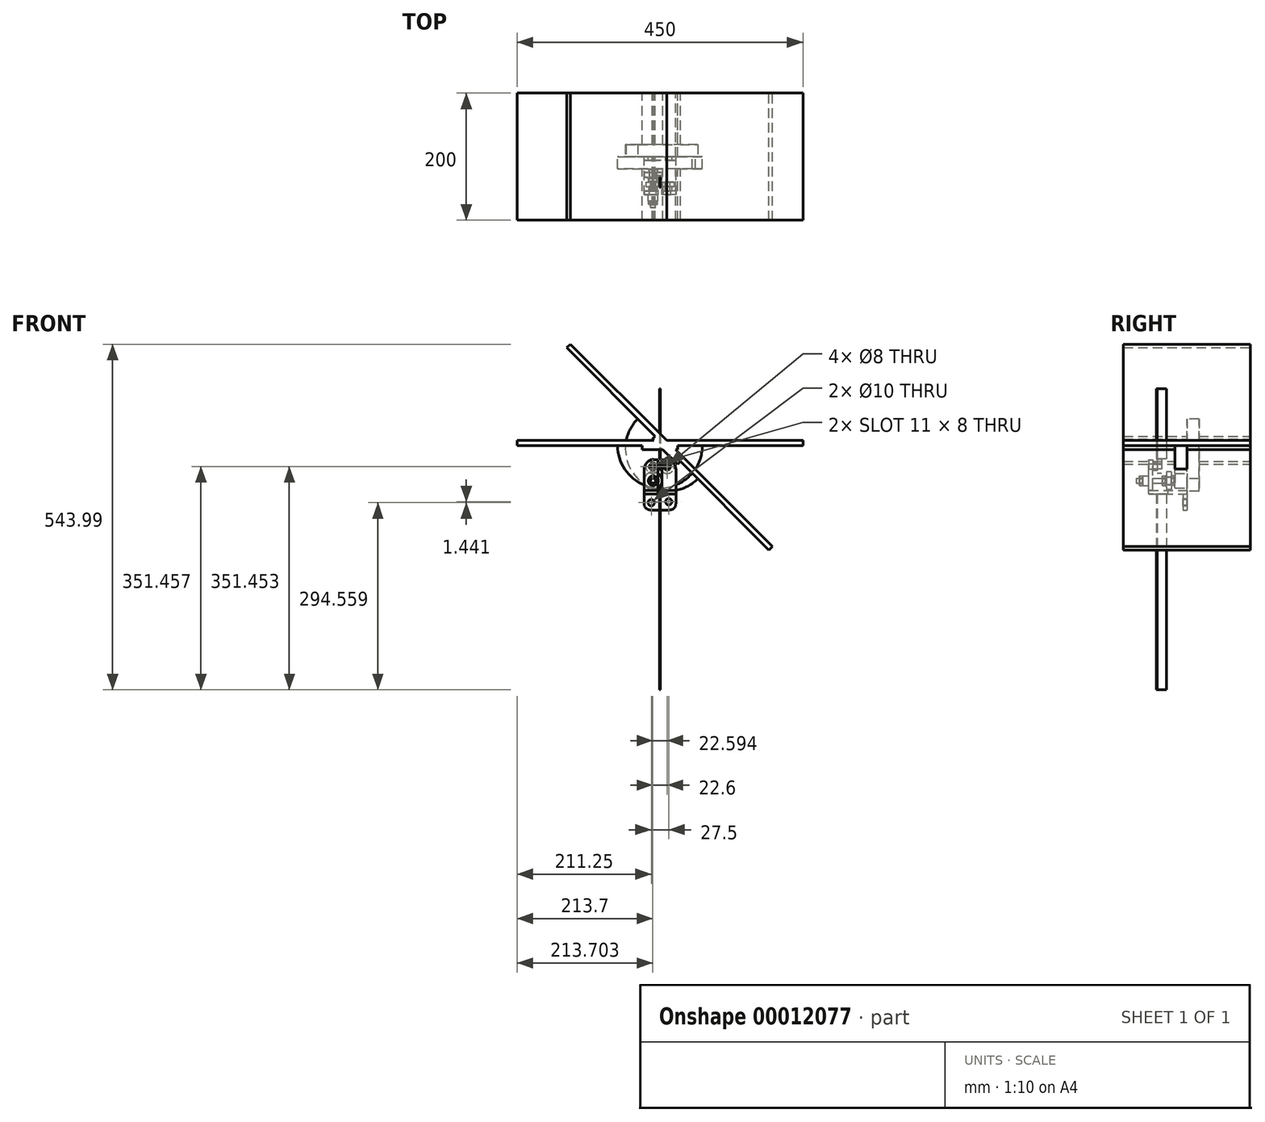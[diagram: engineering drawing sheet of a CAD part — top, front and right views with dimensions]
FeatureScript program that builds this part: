
annotation { "Feature Type Name" : "Feature", "Feature Type Description" : "" }
export const myFeature = defineFeature(function(context is Context, id is Id, definition is map)
    precondition{}
    {
        {
            var Q0;
            Q0=qCreatedBy(makeId("Front.planeOp"),FACE);
            var sketch = newSketch(context, id + "F0", { "sketchPlane" : qUnion([Q0])});
            skLineSegment(sketch, "E0", {"start": v(0, 0) * mm, "end": v(-160.58, 0) * mm, "construction": true});
            skLineSegment(sketch, "E1", {"start": v(-147.95, 0) * mm, "end": v(-147.95, 211) * mm, "construction": true});
            skLineSegment(sketch, "E2", {"start": v(-147.95, 211) * mm, "end": v(0, 367) * mm, "construction": true});
            skLineSegment(sketch, "E3", {"start": v(0, 367) * mm, "end": v(0, 0) * mm, "construction": true});
            skLineSegment(sketch, "E4", {"start": v(-28, 378) * mm, "end": v(28, 378) * mm, "construction": true});
            skLineSegment(sketch, "E5", {"start": v(-225, 384.3) * mm, "end": v(-28, 384.3) * mm, "construction": true});
            skLineSegment(sketch, "E6", {"start": v(28, 384.3) * mm, "end": v(28, 378) * mm, "construction": true});
            skLineSegment(sketch, "E7", {"start": v(-28, 384.3) * mm, "end": v(-28, 378) * mm, "construction": true});
            skLineSegment(sketch, "E8", {"start": v(-225, 392.3) * mm, "end": v(225, 392.3) * mm, "construction": true});
            skLineSegment(sketch, "E9", {"start": v(225, 392.3) * mm, "end": v(225, 384.3) * mm, "construction": true});
            skLineSegment(sketch, "E10", {"start": v(-225, 392.3) * mm, "end": v(-225, 384.3) * mm, "construction": true});
            skLineSegment(sketch, "E11.trimOffspring", {"start": v(28, 384.3) * mm, "end": v(225, 384.3) * mm, "construction": true});
            skCircle(sketch, "E12", {"center": v(0, 367) * mm, "radius": 4 * mm});
            skCircle(sketch, "E13", {"center": v(-147.95, 211) * mm, "radius": 155 * mm});
            skSolve(sketch);
        }
        {
            var Q0;
            Q0=qCreatedBy(makeId("Front.planeOp"),FACE);
            var sketch = newSketch(context, id + "F1", { "sketchPlane" : qUnion([Q0])});
            skLineSegment(sketch, "E14.0", {"start": v(-225, 392.3) * mm, "end": v(225, 392.3) * mm});
            skLineSegment(sketch, "E14.1", {"start": v(-225, 384.3) * mm, "end": v(-28, 384.3) * mm});
            skLineSegment(sketch, "E14.2", {"start": v(-28, 378) * mm, "end": v(28, 378) * mm});
            skLineSegment(sketch, "E14.3", {"start": v(28, 384.3) * mm, "end": v(225, 384.3) * mm});
            skLineSegment(sketch, "E14.4", {"start": v(-225, 392.3) * mm, "end": v(-225, 384.3) * mm});
            skLineSegment(sketch, "E14.5", {"start": v(-28, 384.3) * mm, "end": v(-28, 378) * mm});
            skLineSegment(sketch, "E14.6", {"start": v(28, 384.3) * mm, "end": v(28, 378) * mm});
            skLineSegment(sketch, "E14.7", {"start": v(225, 392.3) * mm, "end": v(225, 384.3) * mm});
            skSolve(sketch);
        }
        {
            var Q0;
            Q0 = qSketchRegion(id + "F1", true);
            var Q1;
            Q1 = qConstructionFilter(qBodyType(qCreatedBy(id + "F1" ,EDGE), BodyType.WIRE), ConstructionObject.NO);
            extrude(context, id + "F2", {"entities" : qUnion([Q0]), "surfaceEntities" : qUnion([Q1]), "depth" : 100 * mm, "hasSecondDirection" : true, "secondDirectionOppositeDirection" : true, "secondDirectionDepth" : 100 * mm});
        }
        {
            var Q0;
            Q0=qCreatedBy(makeId("Front.planeOp"),FACE);
            var sketch = newSketch(context, id + "F3", { "sketchPlane" : qUnion([Q0])});
            skLineSegment(sketch, "E15.1", {"start": v(-225, 392.3) * mm, "end": v(-225, 384.3) * mm});
            skLineSegment(sketch, "E16.7.0", {"start": v(32.03, 359.43) * mm, "end": v(171.33, 220.13) * mm});
            skLineSegment(sketch, "E16.7.1", {"start": v(-12.02, 394.58) * mm, "end": v(27.58, 354.98) * mm});
            skLineSegment(sketch, "E16.7.2", {"start": v(-141.2, 543.99) * mm, "end": v(176.99, 225.8) * mm});
            skLineSegment(sketch, "E16.7.3", {"start": v(-146.87, 538.33) * mm, "end": v(-7.57, 399.03) * mm});
            skLineSegment(sketch, "E16.7.5", {"start": v(32.03, 359.43) * mm, "end": v(27.58, 354.98) * mm});
            skLineSegment(sketch, "E16.7.6", {"start": v(-141.2, 543.99) * mm, "end": v(-146.87, 538.33) * mm});
            skLineSegment(sketch, "E16.7.7", {"start": v(176.99, 225.8) * mm, "end": v(171.33, 220.13) * mm});
            skLineSegment(sketch, "E16.7.8", {"start": v(-7.57, 399.03) * mm, "end": v(-12.02, 394.58) * mm});
            skPoint(sketch, "E16.center", {"position": v(0, 367) * mm});
            skSolve(sketch);
        }
        {
            var Q0;
            Q0 = qSketchRegion(id + "F3", true);
            extrude(context, id + "F4", {"entities" : qUnion([Q0]), "depth" : 100 * mm, "hasSecondDirection" : true, "secondDirectionOppositeDirection" : true, "secondDirectionDepth" : 100 * mm});
        }
        {
            var Q0;
            Q0=qCreatedBy(makeId("Top.planeOp"),FACE);
            var sketch = newSketch(context, id + "F5", { "sketchPlane" : qUnion([Q0])});
            skLineSegment(sketch, "E17.0", {"start": v(0.3, -47.03) * mm, "end": v(0.3, -32.5) * mm});
            skLineSegment(sketch, "E18.0", {"start": v(-0.3, -47.03) * mm, "end": v(-0.3, -32.5) * mm});
            skLineSegment(sketch, "E19", {"start": v(-0.3, -32.5) * mm, "end": v(0.3, -32.5) * mm});
            skLineSegment(sketch, "E20", {"start": v(0.3, -47.03) * mm, "end": v(0.54, -48.4) * mm});
            skLineSegment(sketch, "E21.MirrorCS", {"start": v(-0.3, -47.03) * mm, "end": v(-0.54, -48.4) * mm});
            skLineSegment(sketch, "E22", {"start": v(0, -48.5) * mm, "end": v(0.54, -48.4) * mm});
            skLineSegment(sketch, "E23", {"start": v(0, -48.5) * mm, "end": v(-0.54, -48.4) * mm});
            skSolve(sketch);
        }
        {
            var Q0;
            Q0 = qSketchRegion(id + "F5", true);
            extrude(context, id + "F6", {"entities" : qUnion([Q0]), "depth" : 474 * mm});
        }
        {
            var Q0;
            Q0=qCreatedBy(makeId("Front.planeOp"),FACE);
            var sketch = newSketch(context, id + "F7", { "sketchPlane" : qUnion([Q0])});
            skLineSegment(sketch, "E24.0", {"start": v(-15, 282.96) * mm, "end": v(15, 282.96) * mm});
            skLineSegment(sketch, "E24.1", {"start": v(-25, 308) * mm, "end": v(-25, 292.96) * mm});
            skLineSegment(sketch, "E24.2", {"start": v(25, 308) * mm, "end": v(25, 292.96) * mm});
            skLineSegment(sketch, "E24.3", {"start": v(25, 308) * mm, "end": v(-25, 308) * mm});
            skCircle(sketch, "E24.4", {"center": v(13.75, 296) * mm, "radius": 5 * mm});
            skCircle(sketch, "E24.5", {"center": v(-13.75, 294.56) * mm, "radius": 5 * mm});
            skArc(sketch, "E25.filletArc", {"start": v(-25, 292.96) * mm, "mid": v(-22.07, 285.9) * mm, "end": v(-15, 282.96) * mm});
            skArc(sketch, "E26.filletArc", {"start": v(15, 282.96) * mm, "mid": v(22.07, 285.9) * mm, "end": v(25, 292.96) * mm});
            skSolve(sketch);
        }
        {
            var Q0;
            Q0 = qSketchRegion(id + "F7", true);
            extrude(context, id + "F8", {"entities" : qUnion([Q0]), "depth" : 6 * mm});
        }
        {
            var Q0;
            Q0=qCreatedBy(makeId("Front.planeOp"),FACE);
            var sketch = newSketch(context, id + "F9", { "sketchPlane" : qUnion([Q0])});
            skLineSegment(sketch, "E27.0", {"start": v(25, 308) * mm, "end": v(-25, 308) * mm});
            skLineSegment(sketch, "E28", {"start": v(-25, 308) * mm, "end": v(-25, 314) * mm});
            skLineSegment(sketch, "E29", {"start": v(-25, 314) * mm, "end": v(25, 314) * mm});
            skLineSegment(sketch, "E30", {"start": v(25, 314) * mm, "end": v(25, 308) * mm});
            skPoint(sketch, "E31.orphan", {"position": v(25, 315.71) * mm});
            skSolve(sketch);
        }
        {
            var Q0;
            Q0 = qSketchRegion(id + "F9", true);
            extrude(context, id + "F10", {"entities" : qUnion([Q0]), "depth" : 60 * mm});
        }
        {
            var Q0;
            Q0=makeQuery(id+"F10.opExtrude","CAP_FACE",FACE,{"disambiguationData":[OSD([sQuery(id+"F9.wireOp",EDGE,"E27.0"),sQuery(id+"F9.wireOp",EDGE,"E28"),sQuery(id+"F9.wireOp",EDGE,"E29"),sQuery(id+"F9.wireOp",EDGE,"E30")])],"isStart":false});
            var sketch = newSketch(context, id + "F11", { "sketchPlane" : qUnion([Q0])});
            skLineSegment(sketch, "E32.0", {"start": v(-25, 314) * mm, "end": v(25, 314) * mm});
            skLineSegment(sketch, "E33", {"start": v(-25, 314) * mm, "end": v(-25, 347) * mm});
            skLineSegment(sketch, "E34", {"start": v(25, 314) * mm, "end": v(25, 347) * mm});
            skLineSegment(sketch, "E35", {"start": v(10, 362) * mm, "end": v(-10, 362) * mm});
            skPoint(sketch, "E36.visualSharp", {"position": v(-25, 362) * mm});
            skArc(sketch, "E36.filletArc", {"start": v(-10, 362) * mm, "mid": v(-20.6, 357.6) * mm, "end": v(-25, 347) * mm});
            skPoint(sketch, "E37.visualSharp", {"position": v(25, 362) * mm});
            skArc(sketch, "E37.filletArc", {"start": v(25, 347) * mm, "mid": v(20.6, 357.6) * mm, "end": v(10, 362) * mm});
            skSolve(sketch);
        }
        {
            var Q0;
            Q0 = qSketchRegion(id + "F11", true);
            extrude(context, id + "F12", {"entities" : qUnion([Q0]), "oppositeDirection" : true, "depth" : 6 * mm});
        }
        {
            var Q0;
            Q0=makeQuery(id+"F10.opExtrude","CAP_FACE",FACE,{"disambiguationData":[OSD([sQuery(id+"F9.wireOp",EDGE,"E27.0"),sQuery(id+"F9.wireOp",EDGE,"E28"),sQuery(id+"F9.wireOp",EDGE,"E29"),sQuery(id+"F9.wireOp",EDGE,"E30")])],"isStart":false});
            var sketch = newSketch(context, id + "F13", { "sketchPlane" : qUnion([Q0])});
            skLineSegment(sketch, "E38.0", {"start": v(3, 308) * mm, "end": v(-3, 308) * mm});
            skLineSegment(sketch, "E39.0", {"start": v(3, 308) * mm, "end": v(3, 363.2) * mm});
            skLineSegment(sketch, "E40.0", {"start": v(-3, 308) * mm, "end": v(-3, 363.2) * mm});
            skLineSegment(sketch, "E41", {"start": v(-3, 363.2) * mm, "end": v(3, 363.2) * mm});
            skPoint(sketch, "E42.start.orphan", {"position": v(0, 308) * mm});
            skPoint(sketch, "E43.orphan", {"position": v(25, 308) * mm});
            skPoint(sketch, "E44.orphan", {"position": v(-25, 308) * mm});
            skSolve(sketch);
        }
        {
            var Q0;
            Q0 = qSketchRegion(id + "F13", true);
            extrude(context, id + "F14", {"entities" : qUnion([Q0]), "operationType" : NewBodyOperationType.REMOVE, "oppositeDirection" : true, "depth" : 30 * mm});
        }
        {
            var Q0;
            {var subQ0=sQuery(id+"F11.wireOp",EDGE,"E32.0");var subQ1=sQuery(id+"F11.wireOp",EDGE,"E35");var subQ2=sQuery(id+"F11.wireOp",EDGE,"E33");Q0=makeQuery(id+"F14.boolean.opBoolean","SPLIT",FACE,{"disambiguationData":[TD([makeQuery(id+"F12.opExtrude","SWEPT_FACE",FACE,{"disambiguationData":[OSD([subQ2])]})])],"derivedFrom":makeQuery(id+"F12.opExtrude","CAP_FACE",FACE,{"disambiguationData":[OSD([subQ0,subQ2,sQuery(id+"F11.wireOp",EDGE,"E34"),subQ1])],"isStart":false})});}
            var sketch = newSketch(context, id + "F15", { "sketchPlane" : qUnion([Q0])});
            skCircle(sketch, "E45", {"center": v(10.92, 329) * mm, "radius": 3.4 * mm});
            skCircle(sketch, "E46", {"center": v(10.92, 329) * mm, "radius": 7.5 * mm});
            skSolve(sketch);
        }
        {
            var Q0;
            Q0 = qSketchRegion(id + "F15", true);
            extrude(context, id + "F16", {"entities" : qUnion([Q0]), "oppositeDirection" : true, "depth" : 16 * mm, "hasSecondDirection" : true, "secondDirectionOppositeDirection" : true, "secondDirectionDepth" : 6 * mm});
        }
        {
            var Q0;
            {var subQ0=sQuery(id+"F11.wireOp",EDGE,"E32.0");var subQ1=sQuery(id+"F11.wireOp",EDGE,"E33");var subQ2=sQuery(id+"F11.wireOp",EDGE,"E35");Q0=makeQuery(id+"F14.boolean.opBoolean","SPLIT",FACE,{"disambiguationData":[TD([makeQuery(id+"F12.opExtrude","SWEPT_FACE",FACE,{"disambiguationData":[OSD([subQ1])]})])],"derivedFrom":makeQuery(id+"F12.opExtrude","CAP_FACE",FACE,{"disambiguationData":[OSD([subQ0,subQ1,sQuery(id+"F11.wireOp",EDGE,"E34"),subQ2])],"isStart":false})});}
            var sketch = newSketch(context, id + "F17", { "sketchPlane" : qUnion([Q0])});
            skLineSegment(sketch, "E47.0", {"start": v(46.96, 425.27) * mm, "end": v(-19.08, 359.24) * mm});
            skPoint(sketch, "E48.endSnap0", {"position": v(0, 362) * mm});
            skCircle(sketch, "E49", {"center": v(11.3, 351.46) * mm, "radius": 11 * mm});
            skLineSegment(sketch, "E50.0", {"start": v(0.3, 308) * mm, "end": v(0.3, 373.94) * mm});
            skLineSegment(sketch, "E51.0", {"start": v(-0.3, 308) * mm, "end": v(-0.3, 373.94) * mm});
            skLineSegment(sketch, "E52.0", {"start": v(0, 308) * mm, "end": v(0, 373.94) * mm});
            skCircle(sketch, "E53.MirrorC", {"center": v(-11.3, 351.46) * mm, "radius": 11 * mm});
            skCircle(sketch, "E54", {"center": v(-11.3, 351.46) * mm, "radius": 4 * mm});
            skCircle(sketch, "E55", {"center": v(11.3, 351.46) * mm, "radius": 4 * mm});
            skSolve(sketch);
        }
        {
            var Q0;
            Q0 = qSketchRegion(id + "F17", true);
            extrude(context, id + "F18", {"entities" : qUnion([Q0]), "depth" : 14 * mm, "hasSecondDirection" : true, "secondDirectionOppositeDirection" : false, "secondDirectionDepth" : 7 * mm});
        }
        {
            var Q0;
            Q0=makeQuery(id+"F6.opExtrude","SWEPT_FACE",FACE,{"disambiguationData":[OSD([sQuery(id+"F5.wireOp",EDGE,"E19")])]});
            var sketch = newSketch(context, id + "F19", { "sketchPlane" : qUnion([Q0])});
            skCircle(sketch, "E56", {"center": v(10.92, 329) * mm, "radius": 6 * mm});
            skCircle(sketch, "E57", {"center": v(10.92, 329) * mm, "radius": 14 * mm});
            skSolve(sketch);
        }
        {
            var Q0;
            Q0 = qSketchRegion(id + "F19", true);
            extrude(context, id + "F20", {"entities" : qUnion([Q0]), "depth" : 8 * mm});
        }
        {
            var Q0;
            {var subQ0=sQuery(id+"F11.wireOp",EDGE,"E36.filletArc");var subQ1=sQuery(id+"F11.wireOp",EDGE,"E33");var subQ2=sQuery(id+"F11.wireOp",EDGE,"E35");var subQ3=sQuery(id+"F11.wireOp",EDGE,"E32.0");Q0=makeQuery(id+"F14.boolean.opBoolean","SPLIT",FACE,{"disambiguationData":[TD([makeQuery(id+"F12.opExtrude","SWEPT_FACE",FACE,{"disambiguationData":[OSD([subQ1])]})])],"derivedFrom":makeQuery(id+"F12.opExtrude","CAP_FACE",FACE,{"disambiguationData":[OSD([subQ3,subQ1,sQuery(id+"F11.wireOp",EDGE,"E34"),subQ2,subQ0,sQuery(id+"F11.wireOp",EDGE,"E37.filletArc")])],"isStart":false})});}
            var sketch = newSketch(context, id + "F21", { "sketchPlane" : qUnion([Q0])});
            skCircle(sketch, "E58.1", {"center": v(10.92, 329) * mm, "radius": 3.4 * mm});
            skLineSegment(sketch, "E59", {"start": v(11.3, 347.74) * mm, "end": v(11.3, 347.74) * mm});
            skLineSegment(sketch, "E60", {"start": v(11.3, 355.16) * mm, "end": v(11.3, 355.16) * mm});
            skLineSegment(sketch, "E61", {"start": v(12.8, 355.45) * mm, "end": v(9.8, 355.45) * mm});
            skLineSegment(sketch, "E62", {"start": v(9.8, 347.45) * mm, "end": v(12.8, 347.45) * mm});
            skArc(sketch, "E63.trimOffspring", {"start": v(9.8, 355.45) * mm, "mid": v(5.8, 351.45) * mm, "end": v(9.8, 347.45) * mm});
            skArc(sketch, "E64.trimOffspring", {"start": v(12.8, 347.45) * mm, "mid": v(16.8, 351.45) * mm, "end": v(12.8, 355.45) * mm});
            skArc(sketch, "E65.MirrorCS", {"start": v(-9.8, 355.45) * mm, "mid": v(-5.8, 351.45) * mm, "end": v(-9.8, 347.45) * mm});
            skLineSegment(sketch, "E66.MirrorCS", {"start": v(-12.8, 355.45) * mm, "end": v(-9.8, 355.45) * mm});
            skArc(sketch, "E67.MirrorCS", {"start": v(-12.8, 347.45) * mm, "mid": v(-16.8, 351.45) * mm, "end": v(-12.8, 355.45) * mm});
            skLineSegment(sketch, "E68.MirrorCS", {"start": v(-9.8, 347.45) * mm, "end": v(-12.8, 347.45) * mm});
            skSolve(sketch);
        }
        {
            var Q0;
            Q0 = qSketchRegion(id + "F21", true);
            extrude(context, id + "F22", {"entities" : qUnion([Q0]), "operationType" : NewBodyOperationType.REMOVE, "oppositeDirection" : true, "depth" : 25 * mm});
        }
        {
            var Q0;
            {var subQ0=sQuery(id+"F11.wireOp",EDGE,"E36.filletArc");var subQ1=sQuery(id+"F11.wireOp",EDGE,"E33");var subQ2=sQuery(id+"F11.wireOp",EDGE,"E35");var subQ3=sQuery(id+"F11.wireOp",EDGE,"E32.0");Q0=makeQuery(id+"F14.boolean.opBoolean","SPLIT",FACE,{"disambiguationData":[TD([makeQuery(id+"F12.opExtrude","SWEPT_FACE",FACE,{"disambiguationData":[OSD([subQ1])]})])],"derivedFrom":makeQuery(id+"F12.opExtrude","CAP_FACE",FACE,{"disambiguationData":[OSD([subQ3,subQ1,sQuery(id+"F11.wireOp",EDGE,"E34"),subQ2,subQ0,sQuery(id+"F11.wireOp",EDGE,"E37.filletArc")])],"isStart":false})});}
            var sketch = newSketch(context, id + "F23", { "sketchPlane" : qUnion([Q0])});
            skCircle(sketch, "E69.0", {"center": v(11.3, 351.46) * mm, "radius": 4 * mm});
            skCircle(sketch, "E69.1", {"center": v(-11.3, 351.46) * mm, "radius": 4 * mm});
            skCircle(sketch, "E70", {"center": v(11.3, 351.46) * mm, "radius": 6.75 * mm});
            skCircle(sketch, "E71", {"center": v(-11.3, 351.46) * mm, "radius": 6.75 * mm});
            skSolve(sketch);
        }
        {
            var Q0;
            Q0 = qSketchRegion(id + "F23", true);
            var Q1;
            Q1=makeQuery(id+"F18.opExtrude","CAP_FACE",FACE,{"disambiguationData":[OSD([sQuery(id+"F17.wireOp",EDGE,"E49"),sQuery(id+"F17.wireOp",EDGE,"E55")])],"isStart":true});
            extrude(context, id + "F24", {"entities" : qUnion([Q0]), "endBound" : BoundingType.UP_TO_SURFACE, "endBoundEntityFace" : qUnion([Q1]), "depth" : 25 * mm});
        }
        {
            var Q0;
            Q0=makeQuery(id+"F20.opExtrude","CAP_FACE",FACE,{"disambiguationData":[OSD([sQuery(id+"F19.wireOp",EDGE,"E56"),sQuery(id+"F19.wireOp",EDGE,"E57")])],"isStart":false});
            var sketch = newSketch(context, id + "F25", { "sketchPlane" : qUnion([Q0])});
            skCircle(sketch, "E72.cCircle", {"center": v(10.92, 329) * mm, "radius": 6.5 * mm, "construction": true});
            skLineSegment(sketch, "E72.0", {"start": v(17.73, 325.85) * mm, "end": v(11.6, 321.52) * mm});
            skLineSegment(sketch, "E72.1", {"start": v(11.6, 321.52) * mm, "end": v(4.78, 324.68) * mm});
            skLineSegment(sketch, "E72.2", {"start": v(4.78, 324.68) * mm, "end": v(4.1, 332.15) * mm});
            skLineSegment(sketch, "E72.3", {"start": v(4.1, 332.15) * mm, "end": v(10.24, 336.48) * mm});
            skLineSegment(sketch, "E72.4", {"start": v(10.24, 336.48) * mm, "end": v(17.05, 333.32) * mm});
            skLineSegment(sketch, "E72.5", {"start": v(17.05, 333.32) * mm, "end": v(17.73, 325.85) * mm});
            skPoint(sketch, "E72.0.midPoint", {"position": v(14.66, 323.69) * mm});
            skSolve(sketch);
        }
        {
            var Q0;
            Q0 = qSketchRegion(id + "F25", true);
            extrude(context, id + "F26", {"entities" : qUnion([Q0]), "depth" : 4 * mm});
        }
        {
            var Q0;
            {var subQ0=sQuery(id+"F11.wireOp",EDGE,"E32.0");Q0=makeQuery(id+"F14.boolean.opBoolean","COPY",FACE,{"disambiguationData":[TD([makeQuery(id+"F12.opExtrude","SWEPT_FACE",FACE,{"disambiguationData":[OSD([subQ0])]})])],"derivedFrom":makeQuery(id+"F14.opExtrude","SWEPT_FACE",FACE,{"disambiguationData":[OSD([sQuery(id+"F13.wireOp",EDGE,"E40.0")])]})});}
            cPlane(context, id + "F27", {"entities" : qUnion([Q0]), "cplaneType" : CPlaneType.OFFSET, "offset" : 7.92 * mm, "oppositeDirection" : true, "width" : 150 * mm, "height" : 150 * mm});
        }
        {
            var Q0;
            Q0=qCreatedBy(id+"F27.planeOp",FACE);
            var sketch = newSketch(context, id + "F28", { "sketchPlane" : qUnion([Q0])});
            skLineSegment(sketch, "E73", {"start": v(-18.7, 329) * mm, "end": v(-71.14, 329) * mm, "construction": true});
            skLineSegment(sketch, "E74", {"start": v(-24.92, 335) * mm, "end": v(-24.92, 333) * mm});
            skLineSegment(sketch, "E75", {"start": v(-24.92, 335) * mm, "end": v(-32.5, 335) * mm});
            skLineSegment(sketch, "E76.0", {"start": v(-32.5, 337.49) * mm, "end": v(-32.5, 335) * mm});
            skLineSegment(sketch, "E77", {"start": v(-32.5, 337.49) * mm, "end": v(-34.5, 337.49) * mm});
            skLineSegment(sketch, "E78", {"start": v(-34.5, 337.49) * mm, "end": v(-34.5, 333) * mm});
            skLineSegment(sketch, "E79", {"start": v(-24.92, 333) * mm, "end": v(-34.5, 333) * mm});
            skSolve(sketch);
        }
        {
            var Q0;
            Q0 = qSketchRegion(id + "F28", true);
            var Q1;
            Q1=sQuery(id+"F28.wireOp",EDGE,"E73");
            revolve(context, id + "F29", {"entities" : qUnion([Q0]), "axis" : qUnion([Q1]), "revolveType" : RevolveType.FULL});
        }
        {
            var Q0;
            Q0=makeQuery(id+"F29.opRevolve","SWEPT_FACE",FACE,{"disambiguationData":[OSD([sQuery(id+"F28.wireOp",EDGE,"E78")])]});
            var sketch = newSketch(context, id + "F30", { "sketchPlane" : qUnion([Q0])});
            skCircle(sketch, "E80.cCircle", {"center": v(-10.92, 329) * mm, "radius": 6.5 * mm, "construction": true});
            skLineSegment(sketch, "E80.0", {"start": v(-4.12, 325.82) * mm, "end": v(-10.27, 321.52) * mm});
            skLineSegment(sketch, "E80.1", {"start": v(-10.27, 321.52) * mm, "end": v(-17.07, 324.7) * mm});
            skLineSegment(sketch, "E80.2", {"start": v(-17.07, 324.7) * mm, "end": v(-17.72, 332.18) * mm});
            skLineSegment(sketch, "E80.3", {"start": v(-17.72, 332.18) * mm, "end": v(-11.57, 336.48) * mm});
            skLineSegment(sketch, "E80.4", {"start": v(-11.57, 336.48) * mm, "end": v(-4.77, 333.3) * mm});
            skLineSegment(sketch, "E80.5", {"start": v(-4.77, 333.3) * mm, "end": v(-4.12, 325.82) * mm});
            skPoint(sketch, "E80.0.midPoint", {"position": v(-7.2, 323.67) * mm});
            skCircle(sketch, "E81.0", {"center": v(-10.92, 329) * mm, "radius": 4 * mm});
            skSolve(sketch);
        }
        {
            var Q0;
            Q0 = qSketchRegion(id + "F30", true);
            extrude(context, id + "F31", {"entities" : qUnion([Q0]), "depth" : 4.5 * mm});
        }
        {
            var Q0;
            Q0=qCreatedBy(id+"F27.planeOp",FACE);
            var sketch = newSketch(context, id + "F32", { "sketchPlane" : qUnion([Q0])});
            skLineSegment(sketch, "E82", {"start": v(-24.01, 329) * mm, "end": v(-80.08, 329) * mm});
            skLineSegment(sketch, "E83", {"start": v(-24.01, 333) * mm, "end": v(-80.08, 333) * mm});
            skLineSegment(sketch, "E84", {"start": v(-24.01, 333) * mm, "end": v(-24.01, 329) * mm});
            skLineSegment(sketch, "E85", {"start": v(-80.08, 333) * mm, "end": v(-80.08, 329) * mm});
            skPoint(sketch, "E86.orphan", {"position": v(-80.08, 327.73) * mm});
            skPoint(sketch, "E87.orphan", {"position": v(-24.01, 327.73) * mm});
            skSolve(sketch);
        }
        {
            var Q0;
            Q0 = qSketchRegion(id + "F32", true);
            var Q1;
            Q1=sQuery(id+"F32.wireOp",EDGE,"E82");
            revolve(context, id + "F33", {"operationType" : NewBodyOperationType.ADD, "entities" : qUnion([Q0]), "axis" : qUnion([Q1]), "revolveType" : RevolveType.FULL});
        }
        {
            var Q0;
            Q0=makeQuery(id+"F16.opExtrude","CAP_FACE",FACE,{"disambiguationData":[OSD([sQuery(id+"F15.wireOp",EDGE,"E45"),sQuery(id+"F15.wireOp",EDGE,"E46")])],"isStart":false});
            var sketch = newSketch(context, id + "F34", { "sketchPlane" : qUnion([Q0])});
            skCircle(sketch, "E88.cCircle", {"center": v(-10.92, 329) * mm, "radius": 6.5 * mm, "construction": true});
            skLineSegment(sketch, "E88.0", {"start": v(-4.01, 326.06) * mm, "end": v(-10, 321.55) * mm});
            skLineSegment(sketch, "E88.1", {"start": v(-10, 321.55) * mm, "end": v(-16.91, 324.49) * mm});
            skLineSegment(sketch, "E88.2", {"start": v(-16.91, 324.49) * mm, "end": v(-17.82, 331.94) * mm});
            skLineSegment(sketch, "E88.3", {"start": v(-17.82, 331.94) * mm, "end": v(-11.83, 336.45) * mm});
            skLineSegment(sketch, "E88.4", {"start": v(-11.83, 336.45) * mm, "end": v(-4.92, 333.51) * mm});
            skLineSegment(sketch, "E88.5", {"start": v(-4.92, 333.51) * mm, "end": v(-4.01, 326.06) * mm});
            skPoint(sketch, "E88.0.midPoint", {"position": v(-7, 323.8) * mm});
            skSolve(sketch);
        }
        {
            var Q0;
            Q0 = qSketchRegion(id + "F34", true);
            extrude(context, id + "F35", {"entities" : qUnion([Q0]), "depth" : 5 * mm});
        }
        {
            var Q0;
            Q0=makeQuery(id+"F8.opExtrude","CAP_FACE",FACE,{"disambiguationData":[OSD([sQuery(id+"F7.wireOp",EDGE,"E24.0"),sQuery(id+"F7.wireOp",EDGE,"E24.1"),sQuery(id+"F7.wireOp",EDGE,"E24.2"),sQuery(id+"F7.wireOp",EDGE,"E24.3"),sQuery(id+"F7.wireOp",EDGE,"E24.4"),sQuery(id+"F7.wireOp",EDGE,"E24.5")])],"isStart":true});
            var sketch = newSketch(context, id + "F36", { "sketchPlane" : qUnion([Q0])});
            skLineSegment(sketch, "E89", {"start": v(27.96, 384.14) * mm, "end": v(0, 384.14) * mm, "construction": true});
            skLineSegment(sketch, "E90", {"start": v(0, 378.04) * mm, "end": v(0, 384.14) * mm, "construction": true});
            skArc(sketch, "E91", {"start": v(-66.67, 384.3) * mm, "mid": v(0, 317.47) * mm, "end": v(66.67, 384.3) * mm});
            skLineSegment(sketch, "E92.0", {"start": v(-28, 384.3) * mm, "end": v(-66.67, 384.3) * mm});
            skLineSegment(sketch, "E92.1", {"start": v(-28, 384.3) * mm, "end": v(-28, 378) * mm});
            skLineSegment(sketch, "E92.2", {"start": v(28, 378) * mm, "end": v(-28, 378) * mm});
            skLineSegment(sketch, "E92.3", {"start": v(28, 384.3) * mm, "end": v(28, 378) * mm});
            skLineSegment(sketch, "E92.4", {"start": v(66.67, 384.3) * mm, "end": v(28, 384.3) * mm});
            skPoint(sketch, "E93.orphan", {"position": v(-225, 384.3) * mm});
            skPoint(sketch, "E94.orphan", {"position": v(225, 384.3) * mm});
            skSolve(sketch);
        }
        {
            var Q0;
            Q0 = qSketchRegion(id + "F36", true);
            extrude(context, id + "F37", {"entities" : qUnion([Q0]), "operationType" : NewBodyOperationType.ADD, "oppositeDirection" : true, "depth" : 19 * mm});
        }
        {
            var Q0;
            Q0=makeQuery(id+"F8.opExtrude","CAP_FACE",FACE,{"disambiguationData":[OSD([sQuery(id+"F7.wireOp",EDGE,"E24.0"),sQuery(id+"F7.wireOp",EDGE,"E24.1"),sQuery(id+"F7.wireOp",EDGE,"E24.2"),sQuery(id+"F7.wireOp",EDGE,"E24.3"),sQuery(id+"F7.wireOp",EDGE,"E24.4"),sQuery(id+"F7.wireOp",EDGE,"E24.5"),sQuery(id+"F7.wireOp",EDGE,"E25.filletArc"),sQuery(id+"F7.wireOp",EDGE,"E26.filletArc")])],"isStart":true});
            var sketch = newSketch(context, id + "F38", { "sketchPlane" : qUnion([Q0])});
            skLineSegment(sketch, "E95.0", {"start": v(12.02, 394.58) * mm, "end": v(-27.58, 354.98) * mm});
            skLineSegment(sketch, "E96", {"start": v(-7.78, 374.78) * mm, "end": v(-21.41, 388.41) * mm});
            skLineSegment(sketch, "E97.0", {"start": v(-32.03, 359.43) * mm, "end": v(-59.38, 332.09) * mm});
            skPoint(sketch, "E98.orphan", {"position": v(-32.03, 359.43) * mm});
            skArc(sketch, "E99", {"start": v(-59.38, 332.09) * mm, "mid": v(34.91, 332.09) * mm, "end": v(34.91, 426.38) * mm});
            skLineSegment(sketch, "E100.0", {"start": v(7.57, 399.03) * mm, "end": v(12.02, 394.58) * mm});
            skLineSegment(sketch, "E100.1", {"start": v(34.91, 426.38) * mm, "end": v(7.57, 399.03) * mm});
            skLineSegment(sketch, "E100.2", {"start": v(-32.03, 359.43) * mm, "end": v(-27.58, 354.98) * mm});
            skPoint(sketch, "E101.orphan", {"position": v(-171.33, 220.13) * mm});
            skPoint(sketch, "E102.orphan", {"position": v(146.87, 538.33) * mm});
            skSolve(sketch);
        }
        {
            var Q0;
            Q0 = qSketchRegion(id + "F38", true);
            extrude(context, id + "F39", {"entities" : qUnion([Q0]), "operationType" : NewBodyOperationType.ADD, "depth" : 19 * mm});
        }
    });
